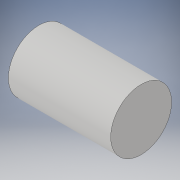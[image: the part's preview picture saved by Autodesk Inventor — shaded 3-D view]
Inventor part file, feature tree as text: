
AUTODESK INVENTOR PART (.ipt)
format: ipt  version: 2017 (Build 210142000, 142)  size: 94,720 bytes
history: native  units: in
note: dims shown in document units (in); Inventor stores cm internally (conversion verified against a paired STEP export)
features: extrude x2, sketch x2
ambient origin geometry x8: Origin, YZ Plane, XZ Plane, XY Plane, X Axis, Y Axis, Z Axis, Center Point
bodies: Solid1 (feature_tree)
feature tree (4):
  extrude  "Extrusion1"  Depth=0.42in TaperAngle=0.0deg
  extrude  "Extrusion2"  [1 undecoded]
  sketch  "Sketch1"  dims[d0=0.25in d1=0.42in d2=0.0in]
  sketch  "Sketch2"  dims[d3=0.3in d4=0.0in]
note: 1 required parameter value undecoded (feature->parameter linkage not recoverable at this tier; creation-order binding heuristic only, values carry confidence <= 0.55)
